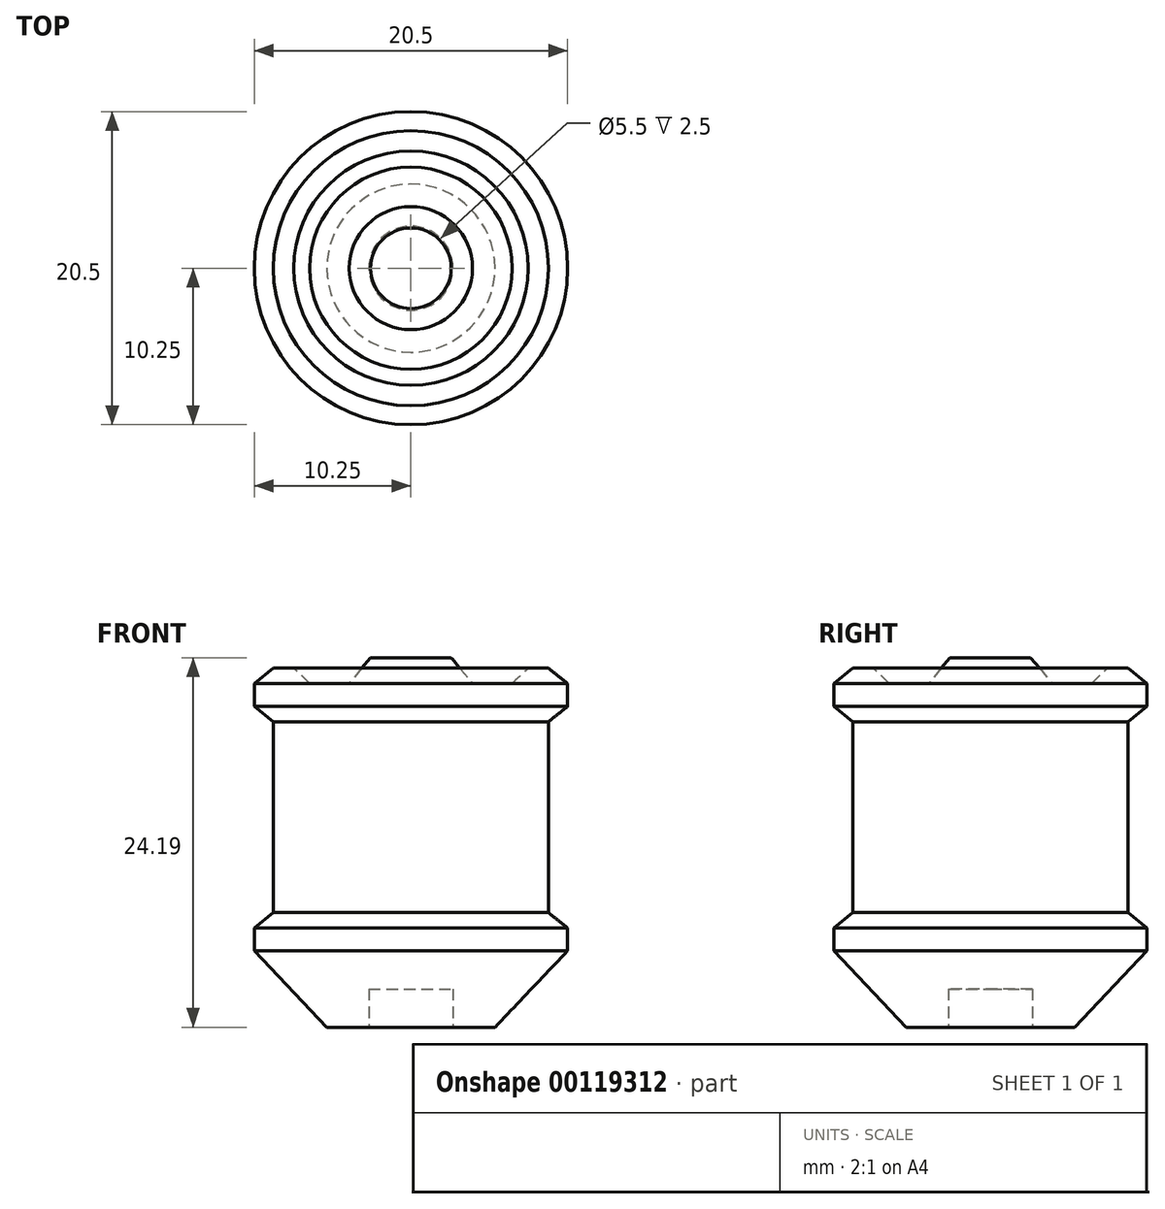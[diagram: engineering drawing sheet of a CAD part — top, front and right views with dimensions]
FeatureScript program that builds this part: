
annotation { "Feature Type Name" : "Feature", "Feature Type Description" : "" }
export const myFeature = defineFeature(function(context is Context, id is Id, definition is map)
    precondition{}
    {
        {
            var Q0;
            Q0=qCreatedBy(makeId("Front.planeOp"),FACE);
            var sketch = newSketch(context, id + "F0", { "sketchPlane" : qUnion([Q0])});
            skLineSegment(sketch, "E0", {"start": v(0, 0) * mm, "end": v(5.5, 0) * mm});
            skLineSegment(sketch, "E1", {"start": v(0, 23.5) * mm, "end": v(0, 0) * mm});
            skLineSegment(sketch, "E2", {"start": v(9, 23.5) * mm, "end": v(10.25, 22.5) * mm});
            skLineSegment(sketch, "E3", {"start": v(10.25, 21) * mm, "end": v(9, 20) * mm});
            skLineSegment(sketch, "E4", {"start": v(9, 7.5) * mm, "end": v(10.25, 6.5) * mm});
            skLineSegment(sketch, "E5", {"start": v(10.25, 5) * mm, "end": v(5.5, 0) * mm});
            skLineSegment(sketch, "E6", {"start": v(9, 20) * mm, "end": v(9, 7.5) * mm});
            skLineSegment(sketch, "E7", {"start": v(10.25, 22.5) * mm, "end": v(10.25, 21) * mm});
            skLineSegment(sketch, "E8", {"start": v(10.25, 6.5) * mm, "end": v(10.25, 5) * mm});
            skLineSegment(sketch, "E9", {"start": v(4.03, 22.51) * mm, "end": v(6.62, 22.51) * mm});
            skLineSegment(sketch, "E10.trimOffspring", {"start": v(7.67, 23.5) * mm, "end": v(9, 23.5) * mm});
            skLineSegment(sketch, "E11", {"start": v(4.03, 22.51) * mm, "end": v(2.64, 24.2) * mm});
            skLineSegment(sketch, "E12", {"start": v(2.64, 24.2) * mm, "end": v(0, 24.2) * mm});
            skLineSegment(sketch, "E13", {"start": v(0, 24.2) * mm, "end": v(0, 23.5) * mm});
            skLineSegment(sketch, "E14", {"start": v(7.67, 23.5) * mm, "end": v(6.62, 22.51) * mm});
            skSolve(sketch);
        }
        {
            var Q0;
            Q0 = qSketchRegion(id + "F0", true);
            var Q1;
            Q1=sQuery(id+"F0.wireOp",EDGE,"E1");
            revolve(context, id + "F1", {"entities" : qUnion([Q0]), "axis" : qUnion([Q1]), "revolveType" : RevolveType.FULL});
        }
        {
            var Q0;
            Q0=makeQuery(id+"F1.opRevolve","SWEPT_FACE",FACE,{"disambiguationData":[OSD([sQuery(id+"F0.wireOp",EDGE,"E0")])]});
            var sketch = newSketch(context, id + "F2", { "sketchPlane" : qUnion([Q0])});
            skCircle(sketch, "E15", {"center": v(0, 0) * mm, "radius": 2.75 * mm});
            skSolve(sketch);
        }
        {
            var Q0;
            Q0 = qSketchRegion(id + "F2", true);
            extrude(context, id + "F3", {"entities" : qUnion([Q0]), "operationType" : NewBodyOperationType.REMOVE, "oppositeDirection" : true, "depth" : 2.5 * mm});
        }
    });
